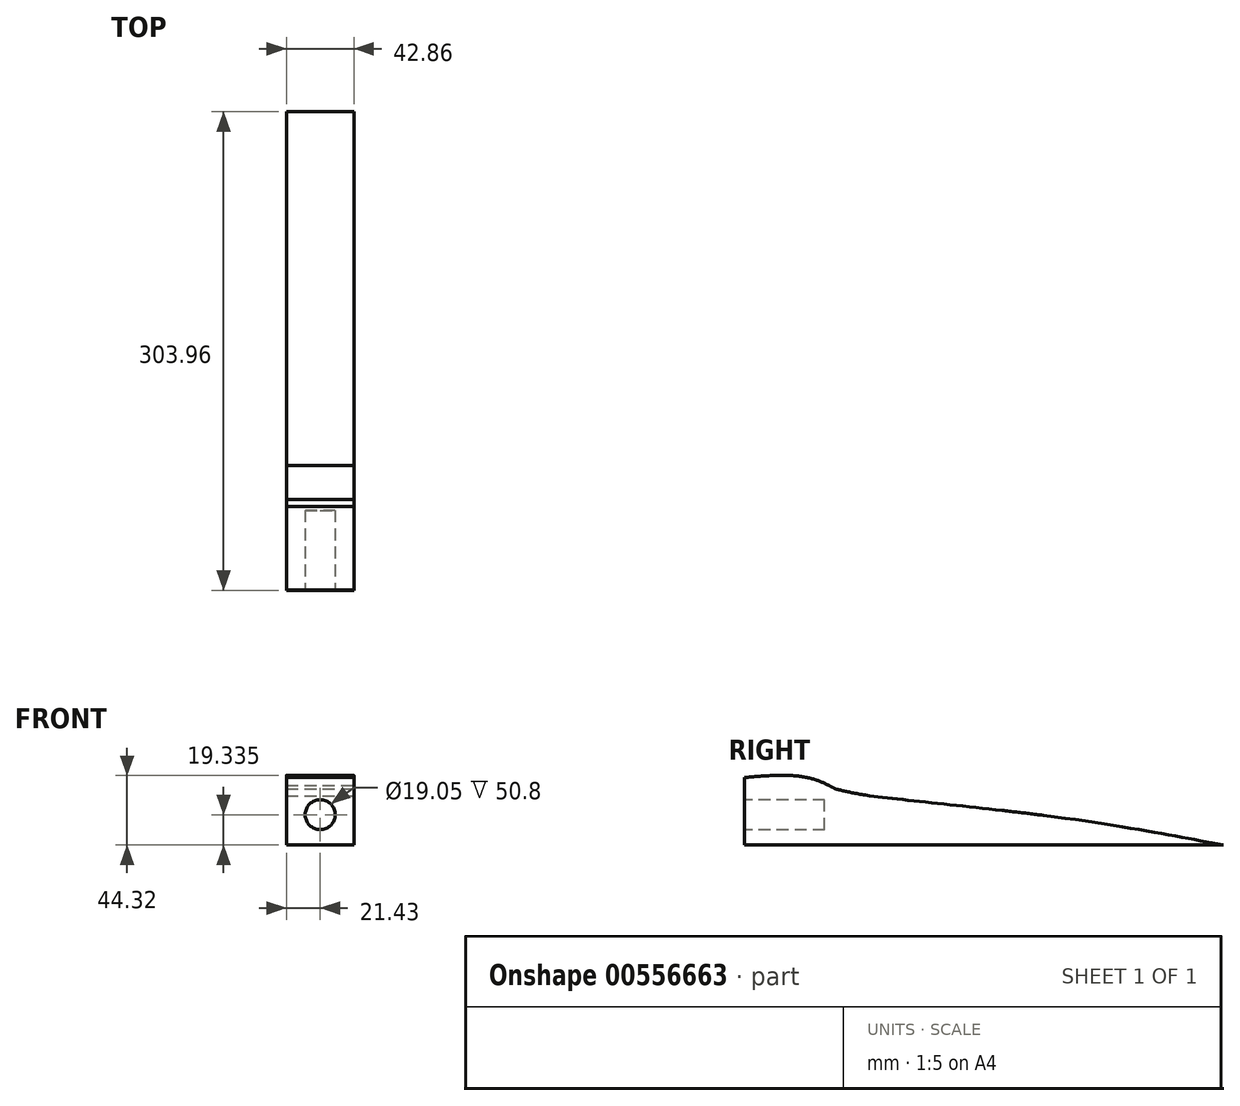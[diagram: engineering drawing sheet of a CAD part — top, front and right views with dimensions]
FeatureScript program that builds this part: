
annotation { "Feature Type Name" : "Feature", "Feature Type Description" : "" }
export const myFeature = defineFeature(function(context is Context, id is Id, definition is map)
    precondition{}
    {
        {
            var Q0;
            Q0=qCreatedBy(makeId("Right.planeOp"),FACE);
            var sketch = newSketch(context, id + "F0", { "sketchPlane" : qUnion([Q0])});
            skLineSegment(sketch, "E0", {"start": v(-152.4, 0) * mm, "end": v(152.4, 0) * mm});
            skLineSegment(sketch, "E1", {"start": v(-152.4, 0) * mm, "end": v(-152.4, 69.85) * mm});
            skLineSegment(sketch, "E2", {"start": v(152.4, 0) * mm, "end": v(152.4, 19.05) * mm});
            skLineSegment(sketch, "E3", {"start": v(152.4, 19.05) * mm, "end": v(-152.4, 69.85) * mm});
            skPoint(sketch, "E4.endSnap0", {"position": v(-152.4, 34.93) * mm});
            skLineSegment(sketch, "E5.0", {"start": v(-95.25, 50.8) * mm, "end": v(-152.4, 50.8) * mm, "construction": true});
            skLineSegment(sketch, "E5.1", {"start": v(-95.25, 50.8) * mm, "end": v(-95.25, 19.05) * mm, "construction": true});
            skLineSegment(sketch, "E5.2", {"start": v(-95.25, 19.05) * mm, "end": v(-152.4, 19.05) * mm, "construction": true});
            skSolve(sketch);
        }
        {
            var Q0;
            Q0=makeQuery(id+"F0.imprint","IMPRINT",FACE,{"disambiguationData":[TD([[makeQuery(id+"F0.imprint","IMPRINT",EDGE,{"derivedFrom":sQuery(id+"F0.wireOp",EDGE,"E0")}),1.0]])]});
            extrude(context, id + "F1", {"entities" : qUnion([Q0]), "depth" : 42.86 * mm, "symmetric" : true});
        }
        {
            var Q0;
            Q0=makeQuery(id+"F1.opExtrude","SWEPT_FACE",FACE,{"disambiguationData":[OSD([sQuery(id+"F0.wireOp",EDGE,"E1")])]});
            var sketch = newSketch(context, id + "F2", { "sketchPlane" : qUnion([Q0])});
            skLineSegment(sketch, "E6", {"start": v(21.43, 34.93) * mm, "end": v(0, 34.93) * mm, "construction": true});
            skCircle(sketch, "E7", {"center": v(0, 34.93) * mm, "radius": 9.53 * mm});
            skSolve(sketch);
        }
        {
            var Q0;
            Q0=makeQuery(id+"F2.imprint","IMPRINT",FACE,{"disambiguationData":[TD([[makeQuery(id+"F2.imprint","IMPRINT",EDGE,{"derivedFrom":sQuery(id+"F2.wireOp",EDGE,"E7")}),1.0]])]});
            var Q1;
            Q1=sQuery(id+"F2.wireOp",EDGE,"E7");
            extrude(context, id + "F3", {"entities" : qUnion([Q0]), "operationType" : NewBodyOperationType.REMOVE, "surfaceEntities" : qUnion([Q1]), "oppositeDirection" : true, "depth" : 50.8 * mm});
        }
        {
            var Q0;
            Q0=makeQuery(id+"F1.opExtrude","CAP_FACE",FACE,{"disambiguationData":[OSD([sQuery(id+"F0.wireOp",EDGE,"E0"),sQuery(id+"F0.wireOp",EDGE,"E1"),sQuery(id+"F0.wireOp",EDGE,"E2"),sQuery(id+"F0.wireOp",EDGE,"E3")])],"isStart":false});
            var sketch = newSketch(context, id + "F4", { "sketchPlane" : qUnion([Q0])});
            skLineSegment(sketch, "E8", {"start": v(-152.4, 34.93) * mm, "end": v(-152.4, 44.45) * mm, "construction": true});
            skLineSegment(sketch, "E9.0", {"start": v(-95.25, 19.05) * mm, "end": v(-152.4, 19.05) * mm, "construction": true});
            skLineSegment(sketch, "E9.1", {"start": v(-95.25, 50.8) * mm, "end": v(-95.25, 19.05) * mm, "construction": true});
            skLineSegment(sketch, "E9.2", {"start": v(-152.4, 50.8) * mm, "end": v(-95.25, 50.8) * mm, "construction": true});
            skLineSegment(sketch, "E10", {"start": v(57.15, 0) * mm, "end": v(57.15, 34.93) * mm, "construction": true});
            skLineSegment(sketch, "E11", {"start": v(-152.4, 44.45) * mm, "end": v(-101.6, 44.45) * mm, "construction": true});
            skLineSegment(sketch, "E12", {"start": v(-101.6, 44.45) * mm, "end": v(-101.6, 25.4) * mm, "construction": true});
            skLineSegment(sketch, "E13", {"start": v(-101.6, 25.4) * mm, "end": v(-152.4, 25.4) * mm, "construction": true});
            skSolve(sketch);
        }
        {
            var Q0;
            Q0=makeQuery(id+"F4.imprint","IMPRINT",FACE,{"disambiguationData":[TD([[makeQuery(id+"F4.imprint","IMPRINT",EDGE,{"derivedFrom":makeQuery(id+"F1.opExtrude","CAP_EDGE",EDGE,{"disambiguationData":[OSD([sQuery(id+"F0.wireOp",EDGE,"E0")])],"isStart":false})}),1.0]])]});
            var sketch = newSketch(context, id + "F5", { "sketchPlane" : qUnion([Q0])});
            skPoint(sketch, "E14.0.internal.orphan", {"position": v(151.58, 0) * mm});
            skPoint(sketch, "E14.2.internal.orphan", {"position": v(-35.24, 0) * mm});
            skFitSpline(sketch, "E15", {"points": [v(-94.63, 51.27) * mm, v(-114.74, 58.91) * mm, v(-152.16, 58.51) * mm], "startDerivative": vector(-42.51, 21.7) * mm, "endDerivative": vector(-71.24, -5.95) * mm});
            skFitSpline(sketch, "E16", {"points": [v(-94.63, 51.27) * mm, v(-73.06, 47) * mm, v(37.24, 34.51) * mm, v(151.56, 15.6) * mm], "startDerivative": vector(94.02, -23.14) * mm, "endDerivative": vector(262.52, -49.12) * mm});
            skFitSpline(sketch, "E17", {"points": [v(-152.16, 58.51) * mm, v(-152.4, 58.51) * mm], "startDerivative": vector(-0.24, 0) * mm, "endDerivative": vector(-0.24, 0) * mm});
            skLineSegment(sketch, "E18", {"start": v(-152.54, 15.6) * mm, "end": v(151.56, 15.6) * mm});
            skFitSpline(sketch, "E19", {"points": [v(151.56, 15.6) * mm, v(115.32, 22.37) * mm, v(37.24, 34.51) * mm, v(-73.06, 47) * mm, v(-94.63, 51.27) * mm, v(-100.74, 54.39) * mm, v(-114.74, 58.91) * mm, v(-138.66, 59.64) * mm, v(-152.16, 58.51) * mm], "startDerivative": vector(-250.82, 47.9) * mm, "endDerivative": vector(-150.48, -15.46) * mm});
            skLineSegment(sketch, "E20", {"start": v(151.56, 15.6) * mm, "end": v(-152.54, 15.6) * mm});
            skCircle(sketch, "E21", {"center": v(50.41, 25.12) * mm, "radius": 1.59 * mm});
            skPoint(sketch, "E22.center.orphan", {"position": v(-131.74, 17.18) * mm});
            skPoint(sketch, "E23.center.orphan", {"position": v(-131.88, 26.7) * mm});
            skCircle(sketch, "E24", {"center": v(-88.36, 25.12) * mm, "radius": 1.59 * mm});
            skSolve(sketch);
        }
        {
            var Q0;
            Q0=qCreatedBy(makeId("Right.planeOp"),FACE);
            cPlane(context, id + "F6", {"entities" : qUnion([Q0]), "cplaneType" : CPlaneType.OFFSET, "offset" : 21.7 * mm, "width" : 150 * mm, "height" : 150 * mm});
        }
        {
            var Q0;
            {var subQ8=sQuery(id+"F5.wireOp",EDGE,"E17");Q0=makeQuery(id+"F5.imprint","IMPRINT",FACE,{"disambiguationData":[TD([[makeQuery(id+"F5.imprint","IMPRINT",EDGE,{"derivedFrom":subQ8}),-1.0]])]});}
            var sketch = newSketch(context, id + "F7", { "sketchPlane" : qUnion([Q0])});
            skSolve(sketch);
        }
        {
            var Q0;
            {var subQ8=sQuery(id+"F5.wireOp",EDGE,"E17");Q0=makeQuery(id+"F5.imprint","IMPRINT",FACE,{"disambiguationData":[TD([[makeQuery(id+"F5.imprint","IMPRINT",EDGE,{"derivedFrom":subQ8}),-1.0]])]});}
            extrude(context, id + "F8", {"entities" : qUnion([Q0]), "operationType" : NewBodyOperationType.REMOVE, "oppositeDirection" : true, "depth" : 56.3 * mm, "offsetDistance" : 25 * mm});
        }
    });
